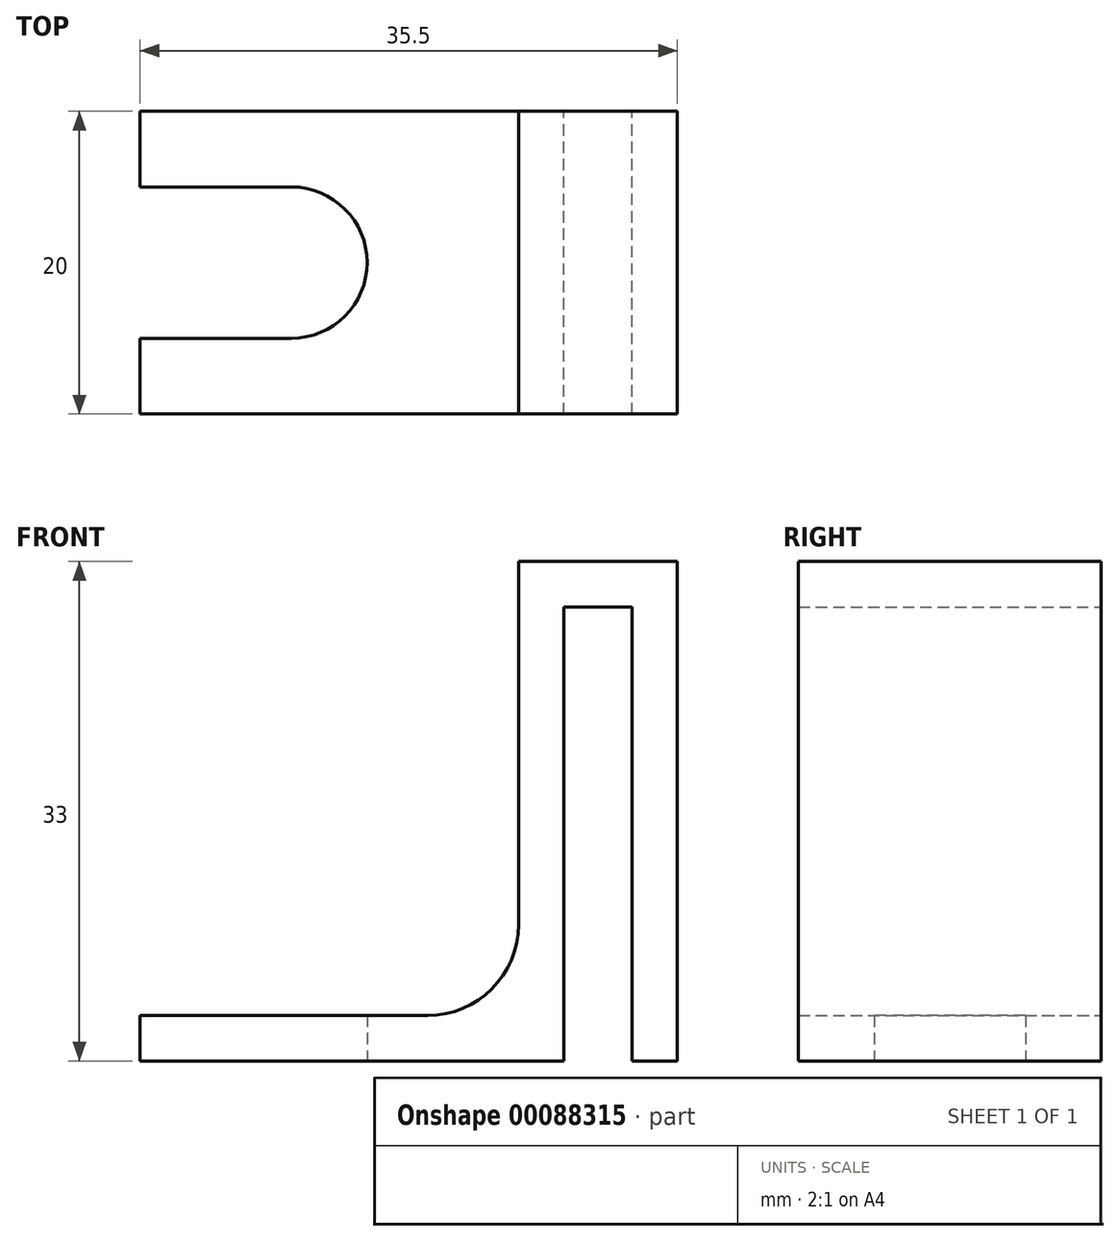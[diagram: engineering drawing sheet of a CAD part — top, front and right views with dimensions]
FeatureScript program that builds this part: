
annotation { "Feature Type Name" : "Feature", "Feature Type Description" : "" }
export const myFeature = defineFeature(function(context is Context, id is Id, definition is map)
    precondition{}
    {
        {
            var Q0;
            Q0=qCreatedBy(makeId("Front.planeOp"),FACE);
            var sketch = newSketch(context, id + "F0", { "sketchPlane" : qUnion([Q0])});
            skLineSegment(sketch, "E0.left", {"start": v(0, 0) * mm, "end": v(0, 3) * mm});
            skLineSegment(sketch, "E1.bottom", {"start": v(0, 0) * mm, "end": v(7.5, 0) * mm});
            skLineSegment(sketch, "E1.top", {"start": v(0, 3) * mm, "end": v(7.5, 3) * mm});
            skLineSegment(sketch, "E1.right", {"start": v(7.5, 0) * mm, "end": v(7.5, 3) * mm});
            skLineSegment(sketch, "E2.bottom", {"start": v(0, 3) * mm, "end": v(3, 3) * mm});
            skLineSegment(sketch, "E2.top", {"start": v(0, -30) * mm, "end": v(3, -30) * mm});
            skLineSegment(sketch, "E2.left", {"start": v(0, 3) * mm, "end": v(0, -30) * mm});
            skLineSegment(sketch, "E2.right", {"start": v(3, 3) * mm, "end": v(3, -30) * mm});
            skLineSegment(sketch, "E3.bottom", {"start": v(7.5, 3) * mm, "end": v(10.5, 3) * mm});
            skLineSegment(sketch, "E3.top", {"start": v(7.5, -30) * mm, "end": v(10.5, -30) * mm});
            skLineSegment(sketch, "E3.left", {"start": v(7.5, 3) * mm, "end": v(7.5, -30) * mm});
            skLineSegment(sketch, "E3.right", {"start": v(10.5, 3) * mm, "end": v(10.5, -30) * mm});
            skLineSegment(sketch, "E4.bottom", {"start": v(0, -30) * mm, "end": v(-25, -30) * mm});
            skLineSegment(sketch, "E4.top", {"start": v(0, -27) * mm, "end": v(-25, -27) * mm});
            skLineSegment(sketch, "E4.left", {"start": v(0, -30) * mm, "end": v(0, -27) * mm});
            skLineSegment(sketch, "E4.right", {"start": v(-25, -30) * mm, "end": v(-25, -27) * mm});
            skPoint(sketch, "E0.bottom.end.orphan", {"position": v(-25, 0) * mm});
            skSolve(sketch);
        }
        {
            var Q0;
            Q0=qSketchRegion(id+"F0",true);
            extrude(context, id + "F1", {"entities" : qUnion([Q0]), "depth" : 10 * mm, "offsetDistance" : 25 * mm, "hasSecondDirection" : true, "secondDirectionOppositeDirection" : true, "secondDirectionDepth" : 10 * mm});
        }
        {
            var Q0;
            Q0=qCreatedBy(makeId("Top.planeOp"),FACE);
            cPlane(context, id + "F2", {"entities" : qUnion([Q0]), "cplaneType" : CPlaneType.OFFSET, "offset" : 20 * mm, "oppositeDirection" : true, "width" : 150 * mm, "height" : 150 * mm});
        }
        {
            var Q0;
            Q0=qCreatedBy(id+"F2.planeOp",FACE);
            var sketch = newSketch(context, id + "F3", { "sketchPlane" : qUnion([Q0])});
            skLineSegment(sketch, "E5.0.0", {"start": v(0, 10) * mm, "end": v(-25, 10) * mm, "construction": true});
            skLineSegment(sketch, "E5.0.1", {"start": v(-25, 10) * mm, "end": v(-25, 5) * mm, "construction": true});
            skLineSegment(sketch, "E5.0.2", {"start": v(-25, -10) * mm, "end": v(0, -10) * mm, "construction": true});
            skLineSegment(sketch, "E5.0.3", {"start": v(0, -10) * mm, "end": v(0, 10) * mm, "construction": true});
            skLineSegment(sketch, "E6.bottom", {"start": v(-10, 0) * mm, "end": v(-25, 0) * mm});
            skLineSegment(sketch, "E6.top", {"start": v(-15, 5) * mm, "end": v(-25, 5) * mm});
            skLineSegment(sketch, "E6.right", {"start": v(-25, 0) * mm, "end": v(-25, 5) * mm});
            skLineSegment(sketch, "E7.MirrorCS", {"start": v(-15, -5) * mm, "end": v(-25, -5) * mm});
            skArc(sketch, "E8", {"start": v(-15, -5) * mm, "mid": v(-10, 0) * mm, "end": v(-15, 5) * mm});
            skLineSegment(sketch, "E9.trimOffspring", {"start": v(-25, -5) * mm, "end": v(-25, -10) * mm, "construction": true});
            skPoint(sketch, "E10.orphan", {"position": v(-10, 5) * mm});
            skPoint(sketch, "E11.orphan", {"position": v(-10, -5) * mm});
            skLineSegment(sketch, "E12", {"start": v(-25, 5) * mm, "end": v(-25, -5) * mm});
            skSolve(sketch);
        }
        {
            var Q0;
            Q0=qSketchRegion(id+"F3",true);
            extrude(context, id + "F4", {"entities" : qUnion([Q0]), "operationType" : NewBodyOperationType.REMOVE, "depth" : 10 * mm, "offsetDistance" : 25 * mm, "hasSecondDirection" : true, "secondDirectionOppositeDirection" : true, "secondDirectionDepth" : 10 * mm});
        }
        {
            var Q0;
            Q0=makeQuery(id+"F1.opExtrude","SWEPT_EDGE",EDGE,{"disambiguationData":[OSD([sQuery(id+"F0.wireOp",EDGE,"E2.left"),sQuery(id+"F0.wireOp",EDGE,"E4.top"),sQuery(id+"F0.wireOp",EDGE,"E4.left")])]});
            fillet(context, id + "F5", {"entities" : qUnion([Q0]), "radius" : 6 * mm, "tangentPropagation" : true, "allowEdgeOverflow" : false});
        }
    });
